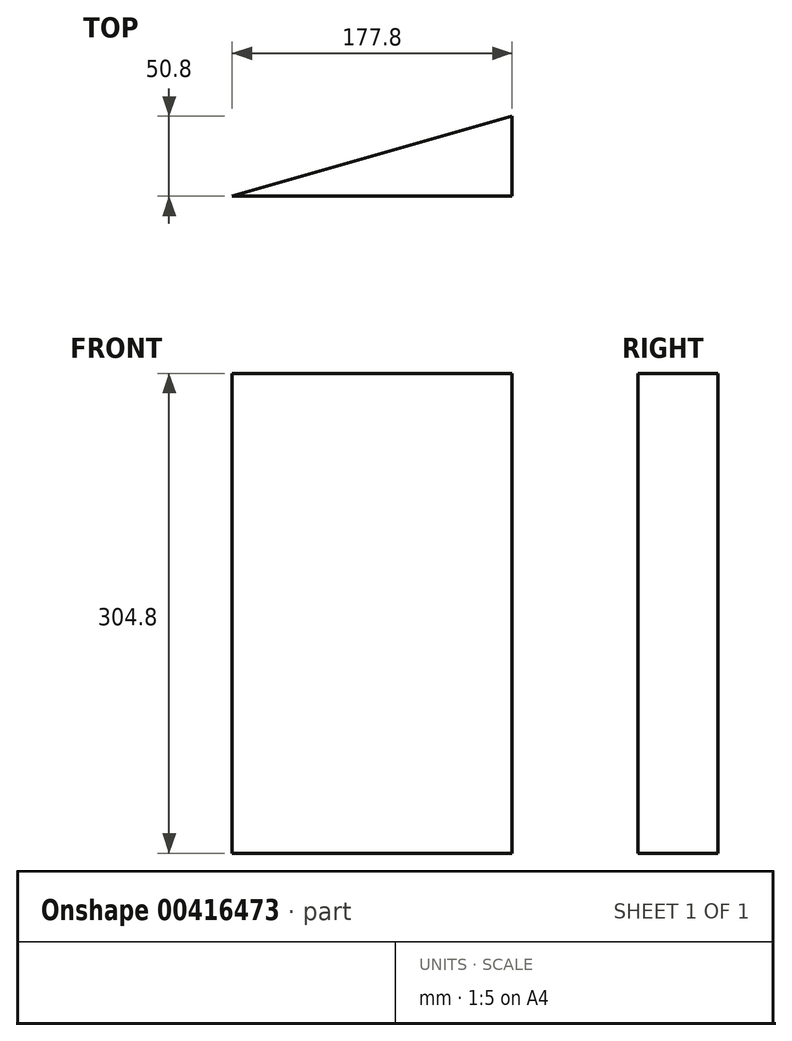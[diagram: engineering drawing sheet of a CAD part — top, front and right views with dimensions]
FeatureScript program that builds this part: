
annotation { "Feature Type Name" : "Feature", "Feature Type Description" : "" }
export const myFeature = defineFeature(function(context is Context, id is Id, definition is map)
    precondition{}
    {
        {
            var Q0;
            Q0=qCreatedBy(makeId("Top.planeOp"),FACE);
            var sketch = newSketch(context, id + "F0", { "sketchPlane" : qUnion([Q0])});
            skLineSegment(sketch, "E0", {"start": v(-82.82, 0) * mm, "end": v(94.98, 0) * mm});
            skLineSegment(sketch, "E1", {"start": v(94.98, 0) * mm, "end": v(94.98, 50.8) * mm});
            skLineSegment(sketch, "E2", {"start": v(94.98, 50.8) * mm, "end": v(-82.82, 0) * mm});
            skSolve(sketch);
        }
        {
            var Q0;
            Q0 = qSketchRegion(id + "F0", true);
            extrude(context, id + "F1", {"entities" : qUnion([Q0]), "depth" : 304.8 * mm});
        }
    });
